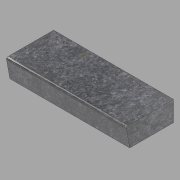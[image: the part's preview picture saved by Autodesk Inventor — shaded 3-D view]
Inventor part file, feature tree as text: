
AUTODESK INVENTOR PART (.ipt)
format: ipt  version: 2022.1 (Build 261234020, 234B)  size: 104,960 bytes
history: native  units: in
note: dims shown in document units (in); Inventor stores cm internally (conversion verified against a paired STEP export)
features: other x3, extrude x1, sketch x1
ambient origin geometry x8: Origin, YZ Plane, XZ Plane, XY Plane, X Axis, Y Axis, Z Axis, Center Point
bodies: Solid1 (feature_tree)
feature tree (5):
  other  "Blocks"
  extrude  "Extrusion1"  Depth=35.625in TaperAngle=0.0deg
  sketch  "Sketch1"  dims[d0=13.0in d1=6.0in d2=13.5in d3=0.5in d4=0.5in d5=35.625in d6=0.0in]
  other  "Profile"
  other  "Profile:1"
